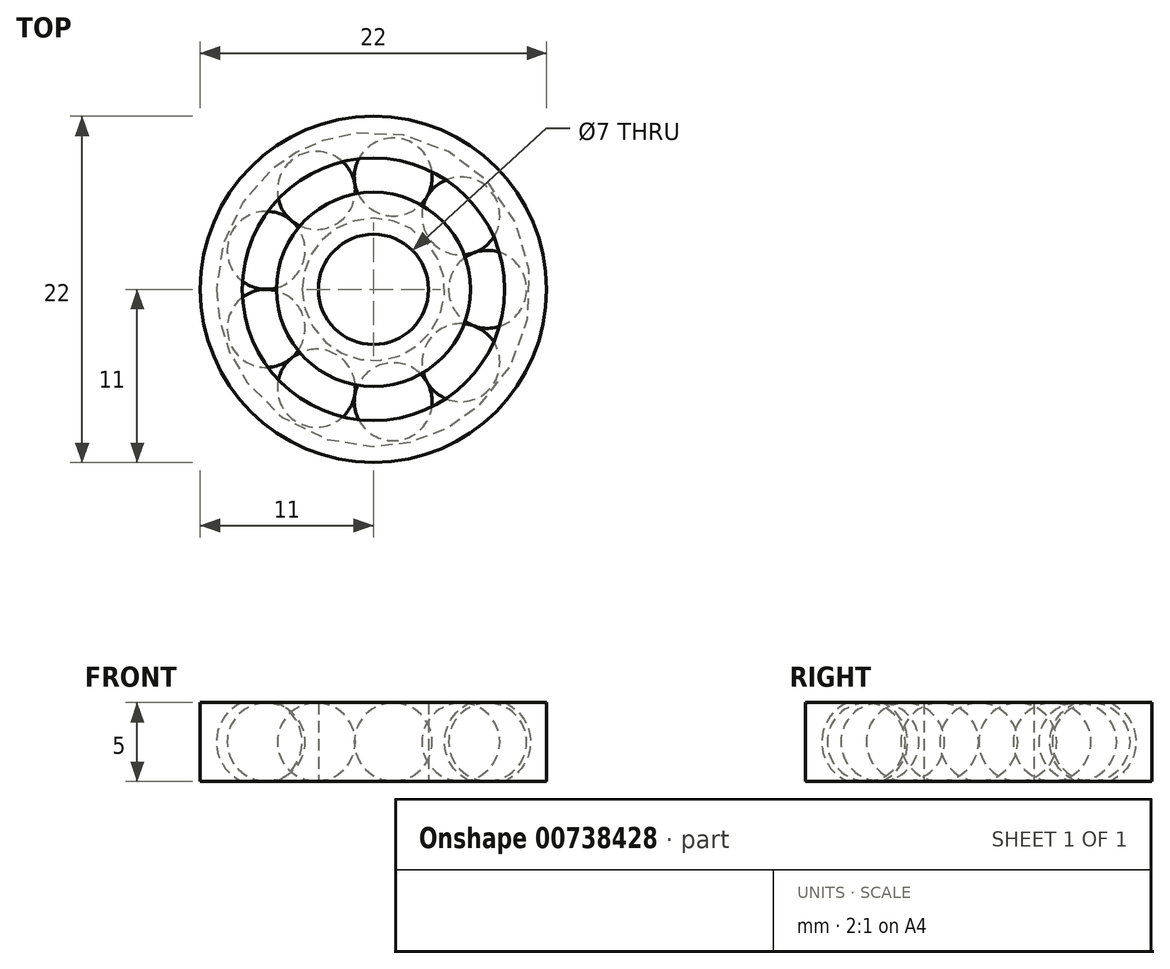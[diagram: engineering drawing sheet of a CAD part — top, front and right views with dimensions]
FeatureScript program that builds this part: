
annotation { "Feature Type Name" : "Feature", "Feature Type Description" : "" }
export const myFeature = defineFeature(function(context is Context, id is Id, definition is map)
    precondition{}
    {
        {
            var Q0;
            Q0=qCreatedBy(makeId("Front.planeOp"),FACE);
            var sketch = newSketch(context, id + "F0", { "sketchPlane" : qUnion([Q0])});
            skLineSegment(sketch, "E0", {"start": v(3.5, 2.5) * mm, "end": v(3.5, -2.5) * mm});
            skLineSegment(sketch, "E1", {"start": v(11, 2.5) * mm, "end": v(11, -2.5) * mm});
            skLineSegment(sketch, "E2", {"start": v(0, 0) * mm, "end": v(3.5, 0) * mm, "construction": true});
            skCircle(sketch, "E3", {"center": v(7.25, 0) * mm, "radius": 2.48 * mm});
            skLineSegment(sketch, "E4", {"start": v(3.5, 0) * mm, "end": v(7.25, 0) * mm, "construction": true});
            skLineSegment(sketch, "E5", {"start": v(11, 0) * mm, "end": v(7.25, 0) * mm, "construction": true});
            skArc(sketch, "E6", {"start": v(6.17, 2.5) * mm, "mid": v(4.52, 0) * mm, "end": v(6.17, -2.5) * mm});
            skArc(sketch, "E7", {"start": v(8.33, 2.5) * mm, "mid": v(9.97, 0) * mm, "end": v(8.33, -2.5) * mm});
            skLineSegment(sketch, "E8", {"start": v(11, 2.5) * mm, "end": v(8.33, 2.5) * mm});
            skLineSegment(sketch, "E9", {"start": v(8.33, -2.5) * mm, "end": v(11, -2.5) * mm});
            skLineSegment(sketch, "E10", {"start": v(6.17, -2.5) * mm, "end": v(3.5, -2.5) * mm});
            skLineSegment(sketch, "E11", {"start": v(3.5, 2.5) * mm, "end": v(6.17, 2.5) * mm});
            skLineSegment(sketch, "E12", {"start": v(0, 0) * mm, "end": v(0, 2.5) * mm, "construction": true});
            skLineSegment(sketch, "E13", {"start": v(0, 0) * mm, "end": v(0, -2.5) * mm, "construction": true});
            skLineSegment(sketch, "E14", {"start": v(7.25, 0) * mm, "end": v(7.25, 2.48) * mm});
            skLineSegment(sketch, "E15", {"start": v(7.25, 0) * mm, "end": v(7.25, -2.48) * mm});
            skSolve(sketch);
        }
        {
            var Q0;
            Q0=makeQuery(id+"F0.imprint","IMPRINT",FACE,{"disambiguationData":[TD([[makeQuery(id+"F0.imprint","IMPRINT",EDGE,{"derivedFrom":sQuery(id+"F0.wireOp",EDGE,"E0")}),1.0]])]});
            var Q1;
            Q1=makeQuery(id+"F0.imprint","IMPRINT",FACE,{"disambiguationData":[TD([[makeQuery(id+"F0.imprint","IMPRINT",EDGE,{"derivedFrom":sQuery(id+"F0.wireOp",EDGE,"E1")}),-1.0]])]});
            var Q2;
            Q2=sQuery(id+"F0.wireOp",EDGE,"E12");
            revolve(context, id + "F1", {"surfaceOperationType" : NewSurfaceOperationType.NEW, "entities" : qUnion([Q0, Q1]), "axis" : qUnion([Q2]), "revolveType" : RevolveType.FULL});
        }
        {
            var Q0;
            {var subQ0=sQuery(id+"F0.wireOp",EDGE,"E14");Q0=makeQuery(id+"F0.imprint","IMPRINT",FACE,{"disambiguationData":[TD([[makeQuery(id+"F0.imprint","IMPRINT",EDGE,{"derivedFrom":subQ0}),-1.0]])]});}
            var Q1;
            Q1=sQuery(id+"F0.wireOp",EDGE,"E14");
            revolve(context, id + "F2", {"surfaceOperationType" : NewSurfaceOperationType.NEW, "entities" : qUnion([Q0]), "axis" : qUnion([Q1]), "revolveType" : RevolveType.FULL});
        }
        {
            var Q0;
            Q0=makeQuery(id+"F2.opRevolve","SWEPT_BODY",BODY,{"disambiguationData":[OSD([sQuery(id+"F0.wireOp",EDGE,"E3"),sQuery(id+"F0.wireOp",EDGE,"E14"),sQuery(id+"F0.wireOp",EDGE,"E15")])]});
            var Q1;
            Q1=makeQuery(id+"F1.opRevolve","SWEPT_FACE",FACE,{"disambiguationData":[OSD([sQuery(id+"F0.wireOp",EDGE,"E0")])]});
            circularPattern(context, id + "F3", {"entities" : qUnion([Q0]), "axis" : qUnion([Q1]), "angle" : 360 * degree, "instanceCount" : 9, "equalSpace" : true});
        }
    });
